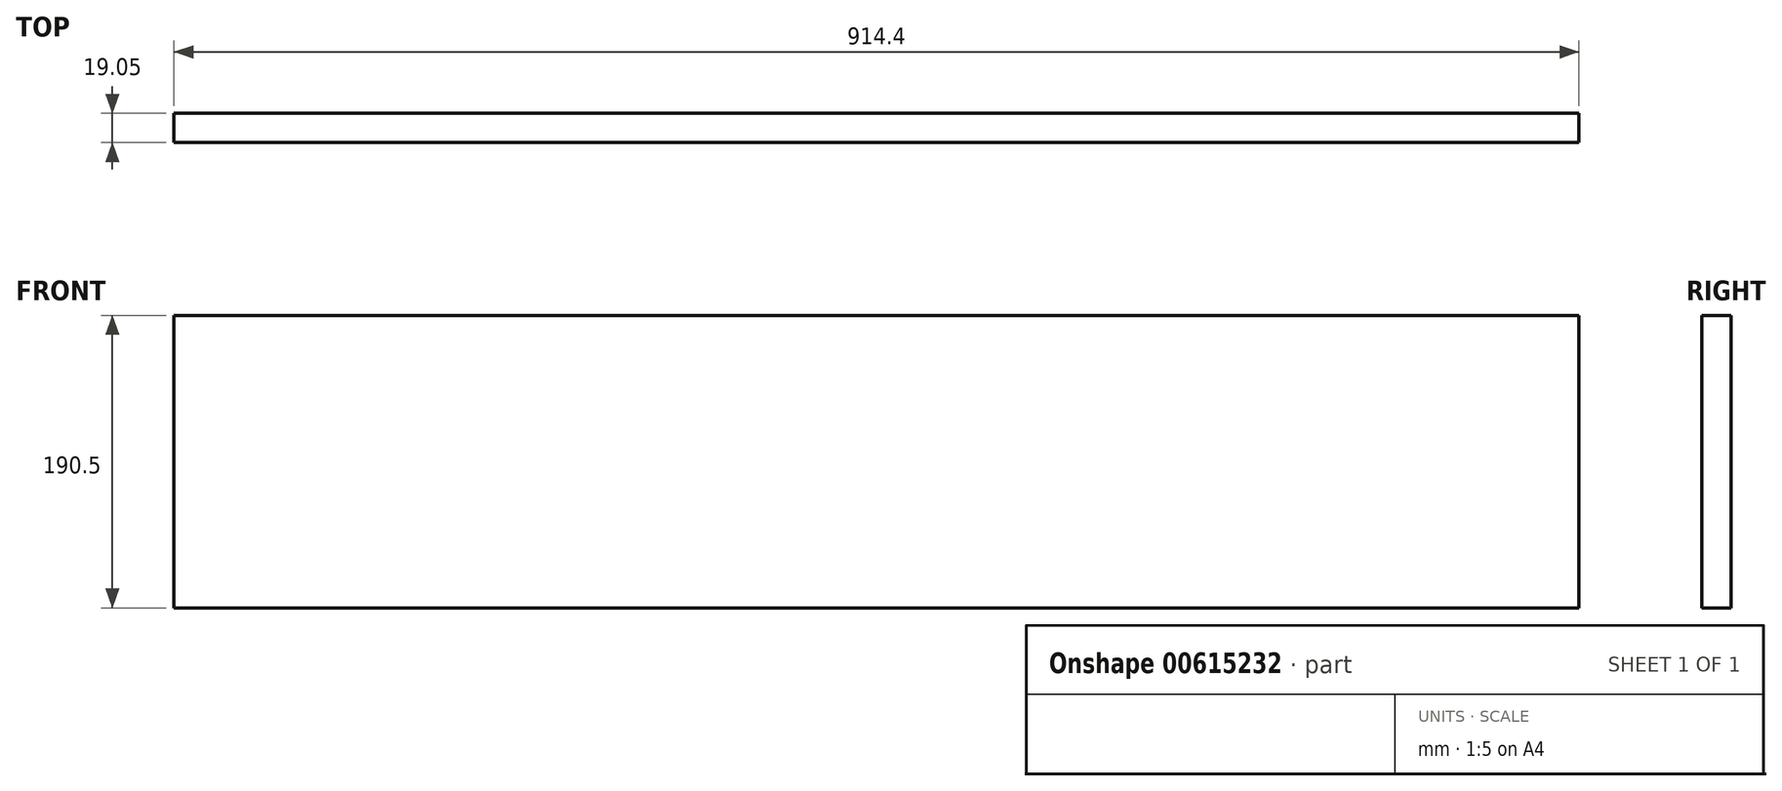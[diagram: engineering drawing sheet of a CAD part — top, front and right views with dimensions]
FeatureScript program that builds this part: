
annotation { "Feature Type Name" : "Feature", "Feature Type Description" : "" }
export const myFeature = defineFeature(function(context is Context, id is Id, definition is map)
    precondition{}
    {
        {
            var Q0;
            Q0=qCreatedBy(makeId("Front.planeOp"),FACE);
            var sketch = newSketch(context, id + "F0", { "sketchPlane" : qUnion([Q0])});
            skLineSegment(sketch, "E0.bottom", {"start": v(0, 0) * mm, "end": v(914.4, 0) * mm});
            skLineSegment(sketch, "E0.top", {"start": v(0, 190.5) * mm, "end": v(914.4, 190.5) * mm});
            skLineSegment(sketch, "E0.left", {"start": v(0, 0) * mm, "end": v(0, 190.5) * mm});
            skLineSegment(sketch, "E0.right", {"start": v(914.4, 0) * mm, "end": v(914.4, 190.5) * mm});
            skSolve(sketch);
        }
        {
            var Q0;
            Q0=makeQuery(id+"F0.imprint","IMPRINT",FACE,{"disambiguationData":[TD([[makeQuery(id+"F0.imprint","IMPRINT",EDGE,{"derivedFrom":sQuery(id+"F0.wireOp",EDGE,"E0.bottom")}),1.0]])]});
            extrude(context, id + "F1", {"entities" : qUnion([Q0]), "depth" : -19.05 * mm, "offsetDistance" : 25.4 * mm});
        }
    });
